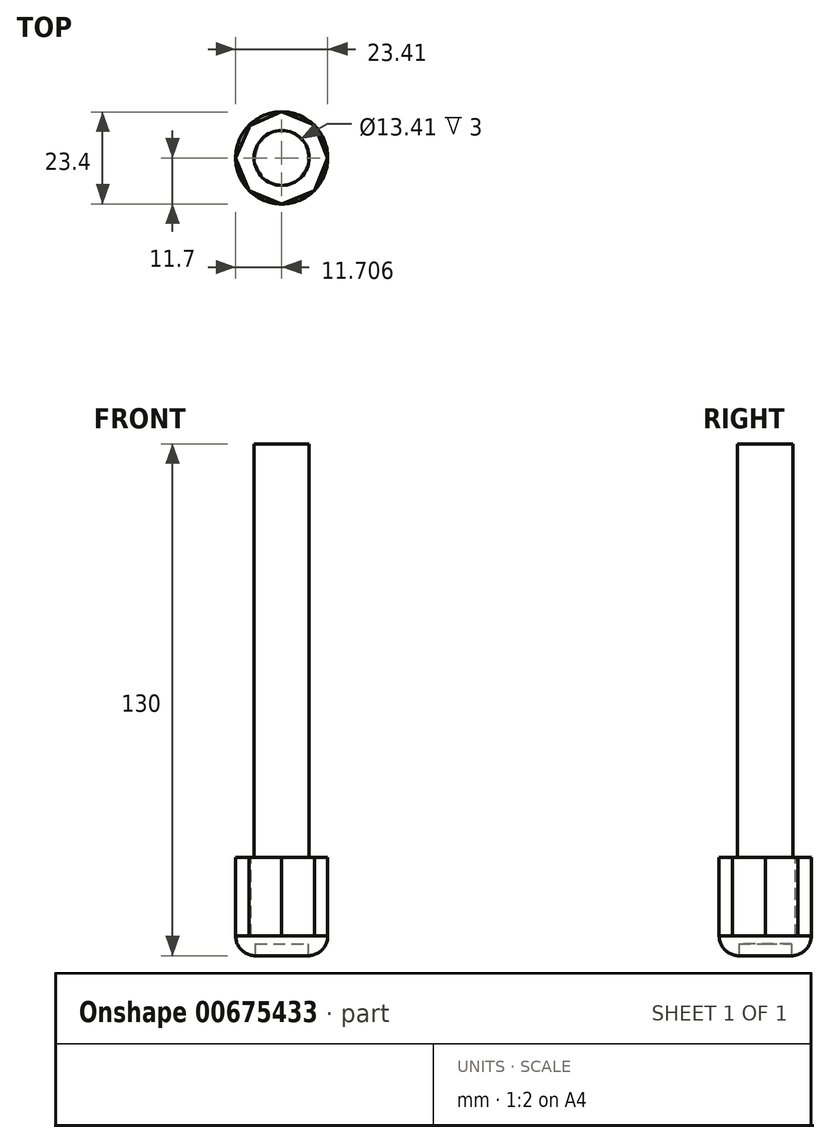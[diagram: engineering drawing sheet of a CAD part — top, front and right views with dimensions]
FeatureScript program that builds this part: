
annotation { "Feature Type Name" : "Feature", "Feature Type Description" : "" }
export const myFeature = defineFeature(function(context is Context, id is Id, definition is map)
    precondition{}
    {
        {
            var Q0;
            Q0=qCreatedBy(makeId("Top.planeOp"),FACE);
            var sketch = newSketch(context, id + "F0", { "sketchPlane" : qUnion([Q0])});
            skCircle(sketch, "E0", {"center": v(-4.65, 0) * mm, "radius": 7 * mm});
            skSolve(sketch);
        }
        {
            var Q0;
            Q0 = qSketchRegion(id + "F0", true);
            extrude(context, id + "F1", {"entities" : qUnion([Q0]), "depth" : 105 * mm, "offsetDistance" : 25 * mm});
        }
        {
            var Q0;
            Q0=makeQuery(id+"F1.opExtrude","CAP_FACE",FACE,{"disambiguationData":[OSD([sQuery(id+"F0.wireOp",EDGE,"E0")])],"isStart":true});
            var sketch = newSketch(context, id + "F2", { "sketchPlane" : qUnion([Q0])});
            skCircle(sketch, "E1", {"center": v(-4.65, 0) * mm, "radius": 11.7 * mm});
            skSolve(sketch);
        }
        {
            var Q0;
            Q0=makeQuery(id+"F2.imprint","IMPRINT",FACE,{"disambiguationData":[TD([[makeQuery(id+"F2.imprint","IMPRINT",EDGE,{"derivedFrom":sQuery(id+"F2.wireOp",EDGE,"E1")}),1.0]])]});
            var Q1;
            Q1=makeQuery(id+"F2.imprint","IMPRINT",FACE,{"disambiguationData":[TD([[makeQuery(id+"F2.imprint","IMPRINT",EDGE,{"derivedFrom":makeQuery(id+"F1.opExtrude","CAP_EDGE",EDGE,{"disambiguationData":[OSD([sQuery(id+"F0.wireOp",EDGE,"E0")])],"isStart":true})}),-1.0]])]});
            extrude(context, id + "F3", {"entities" : qUnion([Q0, Q1]), "operationType" : NewBodyOperationType.ADD, "depth" : 25 * mm, "offsetDistance" : 25 * mm});
        }
        {
            var Q0;
            Q0=makeQuery(id+"F3.opExtrude","CAP_EDGE",EDGE,{"disambiguationData":[OSD([sQuery(id+"F2.wireOp",EDGE,"E1")])],"isStart":false});
            fillet(context, id + "F4", {"entities" : qUnion([Q0]), "radius" : 5 * mm, "tangentPropagation" : true, "allowEdgeOverflow" : false});
        }
        {
            var Q0;
            Q0=makeQuery(id+"F3.opExtrude","CAP_FACE",FACE,{"disambiguationData":[OSD([sQuery(id+"F2.wireOp",EDGE,"E1")])],"isStart":true});
            var sketch = newSketch(context, id + "F5", { "sketchPlane" : qUnion([Q0])});
            skLineSegment(sketch, "E2", {"start": v(-16.36, 0) * mm, "end": v(7.05, 0) * mm});
            skLineSegment(sketch, "E3", {"start": v(7.05, 0) * mm, "end": v(-4.65, 0) * mm});
            skLineSegment(sketch, "E4", {"start": v(-4.65, 0) * mm, "end": v(-4.65, 11.7) * mm});
            skLineSegment(sketch, "E5", {"start": v(-4.65, 11.7) * mm, "end": v(-4.65, -11.7) * mm});
            skLineSegment(sketch, "E6", {"start": v(-4.65, -11.7) * mm, "end": v(-16.36, 0) * mm});
            skLineSegment(sketch, "E7", {"start": v(-16.36, 0) * mm, "end": v(-4.65, 11.7) * mm});
            skLineSegment(sketch, "E8", {"start": v(7.05, 0) * mm, "end": v(-4.65, 11.7) * mm});
            skLineSegment(sketch, "E9", {"start": v(7.05, 0) * mm, "end": v(-4.65, -11.7) * mm});
            skLineSegment(sketch, "E10", {"start": v(-10.5, 5.85) * mm, "end": v(-12.93, 8.28) * mm});
            skLineSegment(sketch, "E11", {"start": v(-12.93, 8.28) * mm, "end": v(3.62, 8.28) * mm});
            skLineSegment(sketch, "E12", {"start": v(3.62, 8.28) * mm, "end": v(3.62, -8.28) * mm});
            skLineSegment(sketch, "E13", {"start": v(3.62, -8.28) * mm, "end": v(-12.93, -8.28) * mm});
            skLineSegment(sketch, "E14", {"start": v(-12.93, -8.28) * mm, "end": v(-12.93, 8.28) * mm});
            skLineSegment(sketch, "E15", {"start": v(-12.74, 8.15) * mm, "end": v(-16.36, 0) * mm});
            skLineSegment(sketch, "E16", {"start": v(-16.36, 0) * mm, "end": v(-12.93, -8.28) * mm});
            skLineSegment(sketch, "E17", {"start": v(-4.65, -11.7) * mm, "end": v(-12.93, -8.28) * mm});
            skLineSegment(sketch, "E18", {"start": v(-4.65, -11.7) * mm, "end": v(3.62, -8.28) * mm});
            skLineSegment(sketch, "E19", {"start": v(7.05, 0) * mm, "end": v(3.62, -8.28) * mm});
            skLineSegment(sketch, "E20", {"start": v(7.05, 0) * mm, "end": v(3.62, 8.28) * mm});
            skLineSegment(sketch, "E21", {"start": v(-4.65, 11.7) * mm, "end": v(3.62, 8.28) * mm});
            skLineSegment(sketch, "E22", {"start": v(-4.65, 11.7) * mm, "end": v(-12.74, 8.15) * mm});
            skSolve(sketch);
        }
        {
            var Q0;
            {var subQ0=sQuery(id+"F5.wireOp",EDGE,"E11");var subQ3=sQuery(id+"F5.wireOp",EDGE,"E22");var subQ4=makeQuery(id+"F5.imprint","INTERSECT",VERTEX,{"derivedFrom":[subQ0,subQ3]});Q0=makeQuery(id+"F5.imprint","IMPRINT",FACE,{"disambiguationData":[TD([[makeQuery(id+"F5.imprint","IMPRINT",EDGE,{"disambiguationData":[TD([[subQ4,1.0]])],"derivedFrom":subQ0}),1.0]])]});}
            var Q1;
            {var subQ0=sQuery(id+"F5.wireOp",EDGE,"E14");var subQ3=sQuery(id+"F5.wireOp",EDGE,"E15");var subQ4=makeQuery(id+"F5.imprint","INTERSECT",VERTEX,{"derivedFrom":[subQ0,subQ3]});Q1=makeQuery(id+"F5.imprint","IMPRINT",FACE,{"disambiguationData":[TD([[makeQuery(id+"F5.imprint","IMPRINT",EDGE,{"disambiguationData":[TD([[subQ4,-1.0]])],"derivedFrom":subQ0}),1.0]])]});}
            var Q2;
            {var subQ0=sQuery(id+"F5.wireOp",EDGE,"E21");Q2=makeQuery(id+"F5.imprint","IMPRINT",FACE,{"disambiguationData":[TD([[makeQuery(id+"F5.imprint","IMPRINT",EDGE,{"derivedFrom":subQ0}),1.0]])]});}
            var Q3;
            {var subQ0=sQuery(id+"F5.wireOp",EDGE,"E20");Q3=makeQuery(id+"F5.imprint","IMPRINT",FACE,{"disambiguationData":[TD([[makeQuery(id+"F5.imprint","IMPRINT",EDGE,{"derivedFrom":subQ0}),-1.0]])]});}
            var Q4;
            {var subQ0=sQuery(id+"F5.wireOp",EDGE,"E19");Q4=makeQuery(id+"F5.imprint","IMPRINT",FACE,{"disambiguationData":[TD([[makeQuery(id+"F5.imprint","IMPRINT",EDGE,{"derivedFrom":subQ0}),1.0]])]});}
            var Q5;
            {var subQ0=sQuery(id+"F5.wireOp",EDGE,"E18");Q5=makeQuery(id+"F5.imprint","IMPRINT",FACE,{"disambiguationData":[TD([[makeQuery(id+"F5.imprint","IMPRINT",EDGE,{"derivedFrom":subQ0}),-1.0]])]});}
            var Q6;
            {var subQ0=sQuery(id+"F5.wireOp",EDGE,"E16");Q6=makeQuery(id+"F5.imprint","IMPRINT",FACE,{"disambiguationData":[TD([[makeQuery(id+"F5.imprint","IMPRINT",EDGE,{"derivedFrom":subQ0}),-1.0]])]});}
            var Q7;
            {var subQ0=sQuery(id+"F5.wireOp",EDGE,"E17");Q7=makeQuery(id+"F5.imprint","IMPRINT",FACE,{"disambiguationData":[TD([[makeQuery(id+"F5.imprint","IMPRINT",EDGE,{"derivedFrom":subQ0}),1.0]])]});}
            extrude(context, id + "F6", {"entities" : qUnion([Q0, Q1, Q2, Q3, Q4, Q5, Q6, Q7]), "operationType" : NewBodyOperationType.REMOVE, "oppositeDirection" : true, "depth" : 20 * mm, "offsetDistance" : 25 * mm});
        }
        {
            var Q0;
            Q0=makeQuery(id+"F3.opExtrude","CAP_FACE",FACE,{"disambiguationData":[OSD([sQuery(id+"F2.wireOp",EDGE,"E1")])],"isStart":false});
            extrude(context, id + "F7", {"entities" : qUnion([Q0]), "operationType" : NewBodyOperationType.REMOVE, "oppositeDirection" : true, "depth" : 3 * mm, "offsetDistance" : 25 * mm});
        }
    });
